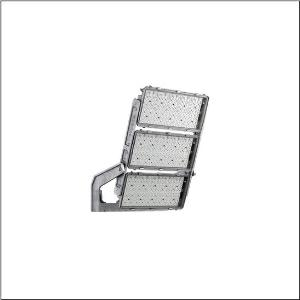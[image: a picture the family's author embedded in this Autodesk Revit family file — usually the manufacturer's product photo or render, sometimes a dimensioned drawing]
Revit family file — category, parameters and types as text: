
# Revit family: floodlight_fl_11_maxi_pro_remote___pl64_5xa779524e01ba_e2b2
name_source: partatom
category: Lighting Fixtures
units: mm (PartAtom-declared; Revit-internal decimal feet)

## family parameters
Cut with Voids When Loaded = No
Host = Face
Light Source = No
Part Type = Normal
Room Calculation Point = No
Round Connector Dimension = Use Diameter
Shared = No

## types (1)
- --- (1 x LED, 107650 lm, 1020.5 W, 5700K)
    Apparent Load = 1020 VA
    CIE Flux Codes = 28 80 98 100 100
    Color Rendering = 90
    Color Temperature = 5700K
    Default Elevation = 1800 mm
    Description = Floodlight FL 11  maxi  pro Remote floodlight; light control with lens of PMMA; cover panel of toughened safety glass, transparent; light distribution: PL64, asymmetric direct distribution, LEDcolour temperature: 5700K, rated luminous flux: 107.650lm, colour rendering: CRI > 90, light colour: 957; luminous efficacy: 106lm/W; brightness control: DMX+RDM; with terminal, 8-pole, max. 2.5mm², mains connection: 220..240V/380..400V AC, 50/60Hz, surge voltage resistance: line to ground: 10kV, ECG replaceable separately, LED unit replaceable without ESD environment, dustproof LED module, dimming range 10..100%; 1021W floodlight with 3x LED unit of diecast aluminium, coated grey; length: 713mm / width: 651mm / height: 338mm; mounting bracket, of diecast aluminium, uncoated, natural, equipment: Longlife, protection rating (complete): IP66; insulation class (complete): insulation class I (protective earthing); certification: CE, ENEC, VDE; ball protection: ball impact resistance with accessories, impact resistance: IK07; only for outdoor installations, rated ambient temperature 10°C, permissible operating ambient temperature: -40..+40°C, permissible storage temperature: -40..+85°C; packaging unit: 1 piece

Light Distribution: PL64
    Height = 320 mm
    Lamp = 1 x LED
    Lamp Light Flux = 107650 lm
    Lamp Power = 1020.5 W
    Lamp count = 1
    Length = 1002 mm
    Luminous efficacy = 105 lm/W
    Manufacturer = Siteco
    ModVariant = No
    Model = 5XA779524E01BA
    Mounting Place = Ceiling
    Mounting Type = Surface mounted
    Number of Poles = 1
    OnlyDefault = Yes
    Power Factor = 1
    Product Name = Floodlight FL 11 maxi pro Remote | PL64
    Product group = floodlight | ceiling mounted
    ProductGroupID = 302
    Protection Class = Protection class I
    Protection Degree = IP 66
    RLX_Detail_Level = 1
    RLX_Emergency_Light_Flux = 0 lm
    RLX_Emergency_Type = 0
    RLX_Emergency_Type_DB = No
    RlxData = <blob elided: 52269 chars, md5=64050bbd>
    Socket = socket
    Standby Power = 0 W
    System Light Flux = 107650 lm
    System Power = 1020 W
    Type Comments = factory setting: luminous flux: 100 % | dim-lin: 255 | 710 mA
    Type Image = l_1006784.jpg
    URL = http://relux.com
    VarID = @adj_027561
    Voltage = 0 V
    Weight = 0.00 kg
    Width = 655 mm

## geometry (parser evidence)
native form markers: Blend x4, Sweep x12
no freeform markers — native parametric forms only
